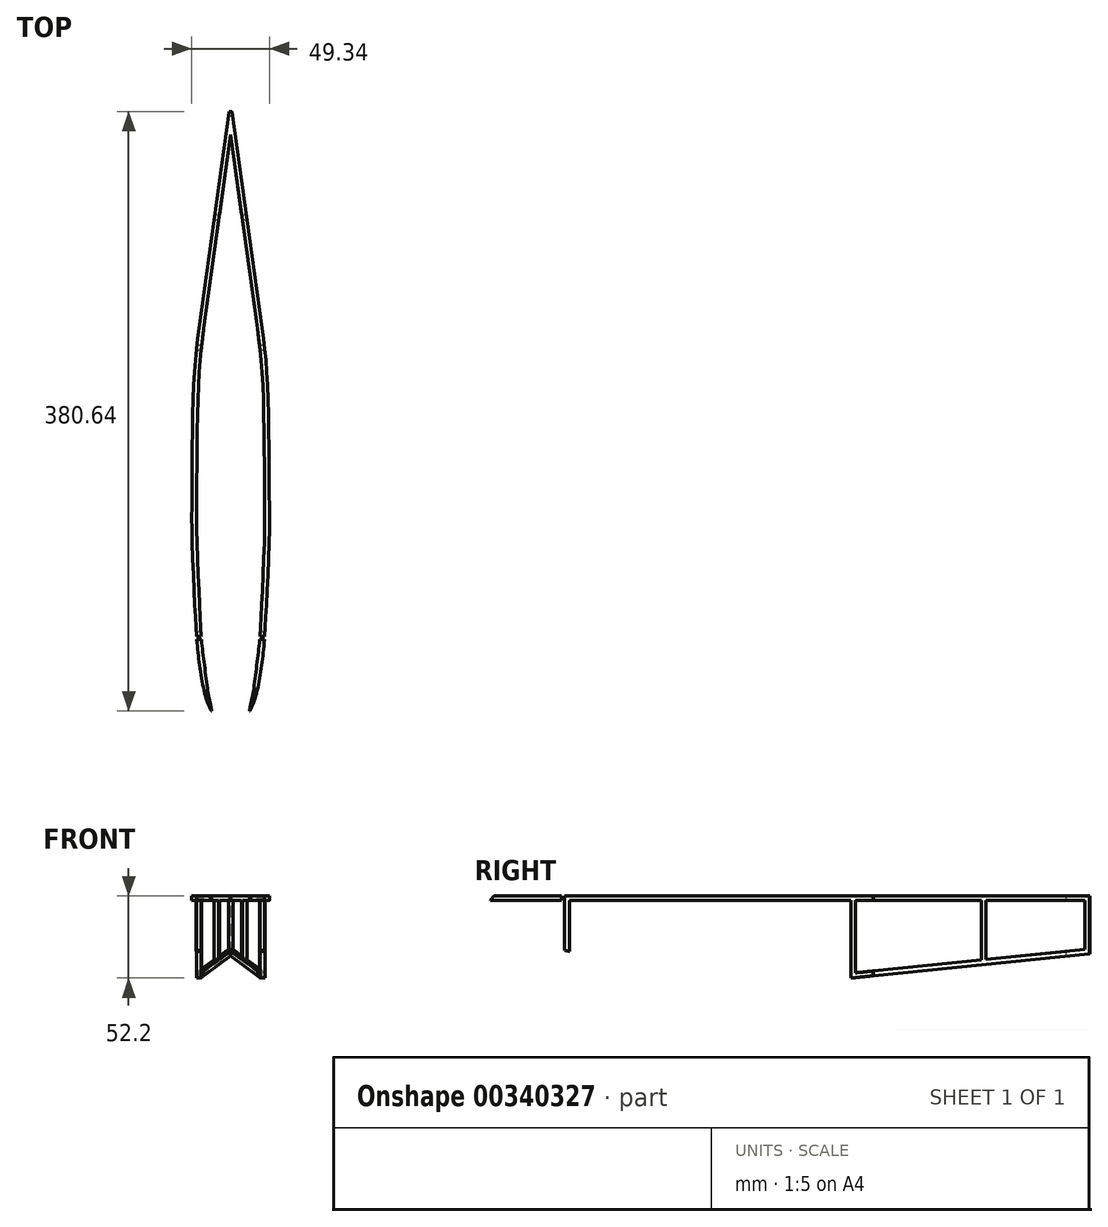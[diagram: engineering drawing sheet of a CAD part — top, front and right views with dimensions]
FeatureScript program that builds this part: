
annotation { "Feature Type Name" : "Feature", "Feature Type Description" : "" }
export const myFeature = defineFeature(function(context is Context, id is Id, definition is map)
    precondition{}
    {
        {
            var Q0;
            Q0=qCreatedBy(makeId("Right.planeOp"),FACE);
            var sketch = newSketch(context, id + "F0", { "sketchPlane" : qUnion([Q0])});
            skLineSegment(sketch, "E0", {"start": v(-181.67, 6.86) * mm, "end": v(153.75, 6.86) * mm});
            skLineSegment(sketch, "E1", {"start": v(153.75, 6.86) * mm, "end": v(153.75, -31.42) * mm});
            skLineSegment(sketch, "E2", {"start": v(153.75, -31.42) * mm, "end": v(2.12, -46.85) * mm});
            skLineSegment(sketch, "E3", {"start": v(-181.67, 6.86) * mm, "end": v(-181.67, -34.5) * mm});
            skLineSegment(sketch, "E4", {"start": v(-47.91, -2.8) * mm, "end": v(-7.67, -2.37) * mm});
            skLineSegment(sketch, "E5", {"start": v(-4.64, -5.37) * mm, "end": v(-4.64, -30.44) * mm});
            skLineSegment(sketch, "E6", {"start": v(-8.1, -33.4) * mm, "end": v(-48.4, -27.13) * mm});
            skLineSegment(sketch, "E7", {"start": v(-50.93, -24.15) * mm, "end": v(-50.88, -5.79) * mm});
            skPoint(sketch, "E8.visualSharp", {"position": v(-50.87, -2.83) * mm});
            skArc(sketch, "E8.filletArc", {"start": v(-47.91, -2.8) * mm, "mid": v(-50, -3.68) * mm, "end": v(-50.88, -5.79) * mm});
            skPoint(sketch, "E9.visualSharp", {"position": v(-50.94, -26.73) * mm});
            skArc(sketch, "E9.filletArc", {"start": v(-50.93, -24.15) * mm, "mid": v(-50.21, -26.11) * mm, "end": v(-48.4, -27.13) * mm});
            skPoint(sketch, "E10.visualSharp", {"position": v(-4.64, -33.95) * mm});
            skArc(sketch, "E10.filletArc", {"start": v(-8.1, -33.4) * mm, "mid": v(-5.69, -32.72) * mm, "end": v(-4.64, -30.44) * mm});
            skPoint(sketch, "E11.visualSharp", {"position": v(-4.64, -2.34) * mm});
            skArc(sketch, "E11.filletArc", {"start": v(-4.64, -5.37) * mm, "mid": v(-5.53, -3.24) * mm, "end": v(-7.67, -2.37) * mm});
            skLineSegment(sketch, "E12", {"start": v(-181.67, 3.86) * mm, "end": v(153.75, 3.86) * mm});
            skLineSegment(sketch, "E13", {"start": v(153.75, -26.9) * mm, "end": v(2.12, -42.32) * mm});
            skLineSegment(sketch, "E14", {"start": v(153.75, -29.91) * mm, "end": v(2.12, -45.34) * mm});
            skLineSegment(sketch, "E15", {"start": v(2.12, -45.34) * mm, "end": v(2.12, -42.32) * mm});
            skLineSegment(sketch, "E16", {"start": v(150.75, -27.2) * mm, "end": v(150.75, 3.86) * mm});
            skLineSegment(sketch, "E17", {"start": v(13.01, -5.1) * mm, "end": v(13.01, -30.7) * mm});
            skLineSegment(sketch, "E18", {"start": v(16.26, -33.7) * mm, "end": v(74.4, -28.8) * mm});
            skLineSegment(sketch, "E19", {"start": v(77.15, -25.8) * mm, "end": v(77.15, -4.88) * mm});
            skLineSegment(sketch, "E20", {"start": v(74.14, -1.88) * mm, "end": v(16, -2.1) * mm});
            skPoint(sketch, "E21.visualSharp", {"position": v(13.01, -2.12) * mm});
            skArc(sketch, "E21.filletArc", {"start": v(16, -2.1) * mm, "mid": v(13.88, -3) * mm, "end": v(13.01, -5.1) * mm});
            skPoint(sketch, "E22.visualSharp", {"position": v(13.01, -33.97) * mm});
            skArc(sketch, "E22.filletArc", {"start": v(13.01, -30.7) * mm, "mid": v(13.98, -32.92) * mm, "end": v(16.26, -33.7) * mm});
            skPoint(sketch, "E23.visualSharp", {"position": v(77.15, -28.57) * mm});
            skArc(sketch, "E23.filletArc", {"start": v(74.4, -28.8) * mm, "mid": v(76.36, -27.84) * mm, "end": v(77.15, -25.8) * mm});
            skPoint(sketch, "E24.visualSharp", {"position": v(77.15, -1.87) * mm});
            skArc(sketch, "E24.filletArc", {"start": v(77.15, -4.88) * mm, "mid": v(76.27, -2.76) * mm, "end": v(74.14, -1.88) * mm});
            skLineSegment(sketch, "E25", {"start": v(84.94, 3.86) * mm, "end": v(84.94, -33.9) * mm});
            skLineSegment(sketch, "E26", {"start": v(87.94, 3.86) * mm, "end": v(87.94, -33.6) * mm});
            skLineSegment(sketch, "E27", {"start": v(2.12, -46.85) * mm, "end": v(2.12, -45.34) * mm});
            skLineSegment(sketch, "E28", {"start": v(2.12, -42.32) * mm, "end": v(2.12, 3.86) * mm});
            skLineSegment(sketch, "E29", {"start": v(5.12, 3.86) * mm, "end": v(5.12, -42.02) * mm});
            skCircle(sketch, "E30", {"center": v(6.62, -40.36) * mm, "radius": 1.5 * mm});
            skArc(sketch, "E31", {"start": v(97.1, 2.65) * mm, "mid": v(95.55, 1.2) * mm, "end": v(97, -0.35) * mm});
            skArc(sketch, "E32", {"start": v(110.86, -0.85) * mm, "mid": v(112.4, 0.6) * mm, "end": v(110.97, 2.15) * mm});
            skLineSegment(sketch, "E33", {"start": v(97.1, 2.65) * mm, "end": v(110.97, 2.15) * mm});
            skLineSegment(sketch, "E34", {"start": v(97, -0.35) * mm, "end": v(110.86, -0.85) * mm});
            skLineSegment(sketch, "E35", {"start": v(96.15, -6.4) * mm, "end": v(96.15, -23.76) * mm});
            skLineSegment(sketch, "E36", {"start": v(99.4, -26.75) * mm, "end": v(141.55, -23.37) * mm});
            skLineSegment(sketch, "E37", {"start": v(144.3, -20.38) * mm, "end": v(144.3, -6.7) * mm});
            skLineSegment(sketch, "E38", {"start": v(141.33, -3.7) * mm, "end": v(99.17, -3.4) * mm});
            skPoint(sketch, "E39.visualSharp", {"position": v(96.15, -3.38) * mm});
            skArc(sketch, "E39.filletArc", {"start": v(99.17, -3.4) * mm, "mid": v(97.04, -4.28) * mm, "end": v(96.15, -6.4) * mm});
            skPoint(sketch, "E40.visualSharp", {"position": v(96.15, -27) * mm});
            skArc(sketch, "E40.filletArc", {"start": v(96.15, -23.76) * mm, "mid": v(97.12, -25.96) * mm, "end": v(99.4, -26.75) * mm});
            skPoint(sketch, "E41.visualSharp", {"position": v(144.3, -23.15) * mm});
            skArc(sketch, "E41.filletArc", {"start": v(141.55, -23.37) * mm, "mid": v(143.51, -22.42) * mm, "end": v(144.3, -20.38) * mm});
            skPoint(sketch, "E42.visualSharp", {"position": v(144.3, -3.72) * mm});
            skArc(sketch, "E42.filletArc", {"start": v(144.3, -6.7) * mm, "mid": v(143.44, -4.58) * mm, "end": v(141.33, -3.7) * mm});
            skLineSegment(sketch, "E43", {"start": v(2.12, -46.85) * mm, "end": v(-9.88, -46.85) * mm});
            skLineSegment(sketch, "E44", {"start": v(-9.88, -46.85) * mm, "end": v(-9.88, -43.2) * mm});
            skLineSegment(sketch, "E45", {"start": v(-9.88, -43.2) * mm, "end": v(2.12, -45.58) * mm});
            skFitSpline(sketch, "E46", {"points": [v(-9.88, -46.85) * mm, v(-40, -44.73) * mm, v(-64.24, -44) * mm, v(-84.8, -44.39) * mm, v(-104.96, -46.05) * mm, v(-118.28, -46.24) * mm, v(-121.99, -46) * mm, v(-124.1, -45.33) * mm, v(-125.1, -44.5) * mm, v(-125.49, -43.66) * mm, v(-125.03, -42.58) * mm, v(-121.9, -40.97) * mm, v(-115.8, -39) * mm, v(-104.8, -36.68) * mm, v(-87.72, -34.92) * mm, v(-76.3, -34.78) * mm, v(-62.3, -35.33) * mm, v(-45.44, -37.09) * mm, v(-20.64, -41.08) * mm, v(-9.88, -43.2) * mm], "startDerivative": vector(-343.17, 26.9) * mm, "endDerivative": vector(173.05, -35.78) * mm});
            skLineSegment(sketch, "E47", {"start": v(-119.74, -40.2) * mm, "end": v(-119.74, -46.2) * mm});
            skLineSegment(sketch, "E48", {"start": v(-125.49, 3.86) * mm, "end": v(-125.49, -43.66) * mm});
            skLineSegment(sketch, "E49.bottom", {"start": v(-111.2, -2.56) * mm, "end": v(-72.11, -2.56) * mm});
            skLineSegment(sketch, "E49.top", {"start": v(-111.2, -27.34) * mm, "end": v(-72.11, -27.34) * mm});
            skLineSegment(sketch, "E49.left", {"start": v(-114.2, -5.56) * mm, "end": v(-114.2, -24.34) * mm});
            skLineSegment(sketch, "E49.right", {"start": v(-69.11, -5.56) * mm, "end": v(-69.11, -24.34) * mm});
            skPoint(sketch, "E50.visualSharp", {"position": v(-114.2, -2.56) * mm});
            skArc(sketch, "E50.filletArc", {"start": v(-111.2, -2.56) * mm, "mid": v(-113.32, -3.44) * mm, "end": v(-114.2, -5.56) * mm});
            skPoint(sketch, "E51.visualSharp", {"position": v(-114.2, -27.34) * mm});
            skArc(sketch, "E51.filletArc", {"start": v(-114.2, -24.34) * mm, "mid": v(-113.32, -26.46) * mm, "end": v(-111.2, -27.34) * mm});
            skPoint(sketch, "E52.visualSharp", {"position": v(-69.11, -27.34) * mm});
            skArc(sketch, "E52.filletArc", {"start": v(-72.11, -27.34) * mm, "mid": v(-69.99, -26.46) * mm, "end": v(-69.11, -24.34) * mm});
            skPoint(sketch, "E53.visualSharp", {"position": v(-69.11, -2.56) * mm});
            skArc(sketch, "E53.filletArc", {"start": v(-69.11, -5.56) * mm, "mid": v(-69.99, -3.44) * mm, "end": v(-72.11, -2.56) * mm});
            skLineSegment(sketch, "E54", {"start": v(-55.36, 3.86) * mm, "end": v(-55.36, -35.9) * mm});
            skLineSegment(sketch, "E55", {"start": v(-57.36, 3.86) * mm, "end": v(-57.36, -35.7) * mm});
            skFitSpline(sketch, "E56", {"points": [v(2.12, -40.57) * mm, v(-16.08, -36.4) * mm, v(-46.24, -31.25) * mm, v(-69.78, -29.1) * mm, v(-81.85, -28.82) * mm, v(-101.5, -30.15) * mm, v(-112.18, -32.12) * mm, v(-119.26, -34.2) * mm, v(-125.49, -36.64) * mm], "startDerivative": vector(-122.16, 29.48) * mm, "endDerivative": vector(-74.05, -30.55) * mm});
            skLineSegment(sketch, "E57", {"start": v(-77.75, -34.76) * mm, "end": v(-77.75, -38.76) * mm});
            skLineSegment(sketch, "E58", {"start": v(-77.75, -38.76) * mm, "end": v(-73.75, -38.76) * mm});
            skLineSegment(sketch, "E59", {"start": v(-73.75, -38.76) * mm, "end": v(-73.75, -34.84) * mm});
            skLineSegment(sketch, "E60", {"start": v(-179.67, 3.86) * mm, "end": v(-179.67, -35.22) * mm});
            skLineSegment(sketch, "E61", {"start": v(-127.49, 3.86) * mm, "end": v(-127.49, -45.88) * mm});
            skLineSegment(sketch, "E62", {"start": v(-127.49, -38.43) * mm, "end": v(-179.67, -27.75) * mm});
            skCircle(sketch, "E63", {"center": v(-128.99, -36.6) * mm, "radius": 1.5 * mm});
            skLineSegment(sketch, "E64", {"start": v(-176.67, 3.86) * mm, "end": v(-176.67, -28.37) * mm});
            skLineSegment(sketch, "E65", {"start": v(-181.67, 6.86) * mm, "end": v(-181.67, 19.81) * mm});
            skLineSegment(sketch, "E66", {"start": v(-181.67, 19.81) * mm, "end": v(-179.67, 19.81) * mm});
            skLineSegment(sketch, "E67", {"start": v(-179.67, 19.81) * mm, "end": v(-179.67, 6.86) * mm});
            skLineSegment(sketch, "E68", {"start": v(-179.67, 6.86) * mm, "end": v(-179.67, 3.86) * mm});
            skLineSegment(sketch, "E69", {"start": v(-179.67, 19.81) * mm, "end": v(-58.12, 19.81) * mm});
            skFitSpline(sketch, "E70", {"points": [v(-58.12, 19.81) * mm, v(-55.87, 16.49) * mm, v(-51.87, 13.82) * mm, v(-44.68, 11.1) * mm, v(-38.76, 9.83) * mm, v(-34.72, 9.5) * mm, v(-32.9, 9.46) * mm, v(-31.68, 8.98) * mm, v(-31.2, 8.18) * mm, v(-31.04, 6.86) * mm], "startDerivative": vector(15.95, -28.34) * mm, "endDerivative": vector(1.18, -19.42) * mm});
            skPoint(sketch, "E71.9.internal.snap0", {"position": v(-13.96, 6.86) * mm});
            skFitSpline(sketch, "E71", {"points": [v(-181.67, 19.81) * mm, v(-183.41, 18.39) * mm, v(-187.18, 16.28) * mm, v(-194, 13.94) * mm, v(-199.88, 12.47) * mm, v(-206.36, 11.53) * mm, v(-212.31, 11) * mm, v(-216.9, 10.25) * mm, v(-221.13, 8.93) * mm, v(-224.44, 6.86) * mm, v(-226.33, 4.9) * mm, v(-227.04, 3.36) * mm, v(-227.27, 0.8) * mm, v(-226.87, -1.76) * mm, v(-225.22, -5.47) * mm, v(-221.64, -10.05) * mm, v(-215.45, -15.6) * mm, v(-203.85, -23.7) * mm, v(-194.52, -28.9) * mm, v(-181.67, -34.5) * mm, v(-165.17, -39.5) * mm, v(-153.07, -41.9) * mm, v(-135.2, -44.8) * mm, v(-127.49, -45.88) * mm, v(-125.49, -46.02) * mm], "startDerivative": vector(-63.83, -56.2) * mm, "endDerivative": vector(74.87, -4.7) * mm});
            skLineSegment(sketch, "E72", {"start": v(-125.49, -46.02) * mm, "end": v(-125.49, -43.66) * mm});
            skLineSegment(sketch, "E73", {"start": v(-181.67, 6.86) * mm, "end": v(-224.44, 6.86) * mm});
            skLineSegment(sketch, "E74", {"start": v(-181.67, 3.86) * mm, "end": v(-226.89, 3.86) * mm});
            skLineSegment(sketch, "E75", {"start": v(-125.7, -48) * mm, "end": v(-131.67, -47.35) * mm});
            skLineSegment(sketch, "E76", {"start": v(-131.67, -47.35) * mm, "end": v(-131.45, -45.37) * mm});
            skLineSegment(sketch, "E77", {"start": v(-125.7, -48) * mm, "end": v(-125.49, -46.02) * mm});
            skFitSpline(sketch, "E78", {"points": [v(-125.49, -44.33) * mm, v(-127.49, -44.12) * mm, v(-140.7, -42.33) * mm, v(-160.51, -38.82) * mm, v(-171.33, -36.19) * mm, v(-179.67, -33.56) * mm, v(-181.67, -32.9) * mm], "startDerivative": vector(-19.3, 1.8) * mm, "endDerivative": vector(-19.46, 6.5) * mm});
            skFitSpline(sketch, "E79", {"points": [v(-181.67, -32.9) * mm, v(-188.4, -30.56) * mm, v(-198.45, -26.86) * mm], "startDerivative": vector(-14.26, 4.84) * mm, "endDerivative": vector(-19.1, 7.25) * mm});
            skLineSegment(sketch, "E80", {"start": v(-181.67, -18.47) * mm, "end": v(-214.55, -16.3) * mm});
            skLineSegment(sketch, "E81", {"start": v(-104.96, -46.05) * mm, "end": v(-9.88, -46.85) * mm});
            skLineSegment(sketch, "E82", {"start": v(153.75, 9.86) * mm, "end": v(153.75, 6.86) * mm});
            skLineSegment(sketch, "E83", {"start": v(153.75, 9.86) * mm, "end": v(76.63, 9.86) * mm});
            skArc(sketch, "E84", {"start": v(76.63, 9.86) * mm, "mid": v(75.13, 8.36) * mm, "end": v(76.63, 6.86) * mm});
            skFitSpline(sketch, "E85", {"points": [v(89.9, 9.86) * mm, v(58.05, 12.78) * mm, v(25.06, 16.1) * mm, v(1.18, 18.57) * mm], "startDerivative": vector(-90.45, 8.07) * mm, "endDerivative": vector(-75.96, 7.86) * mm});
            skFitSpline(sketch, "E86", {"points": [v(1.18, 18.57) * mm, v(0, 14.86) * mm, v(-1.7, 11.63) * mm, v(-3.87, 9.14) * mm, v(-6.2, 7.64) * mm, v(-7.3, 7.32) * mm, v(-8.32, 7.22) * mm, v(-9.2, 7.24) * mm, v(-9.58, 7.12) * mm, v(-9.7, 6.86) * mm], "startDerivative": vector(-6.18, -22.1) * mm, "endDerivative": vector(-1.74, -6.23) * mm});
            skFitSpline(sketch, "E87", {"points": [v(1.18, 18.57) * mm, v(0.28, 21.52) * mm, v(0.14, 24.9) * mm, v(0.78, 27.64) * mm, v(2.27, 29.53) * mm], "startDerivative": vector(-4.12, 11.13) * mm, "endDerivative": vector(7.44, 7.67) * mm});
            skFitSpline(sketch, "E88", {"points": [v(2.27, 29.53) * mm, v(11.3, 28.6) * mm, v(21.09, 26.4) * mm, v(32.75, 22.66) * mm, v(40.6, 19.5) * mm, v(54.25, 13.15) * mm], "startDerivative": vector(49.49, -3.82) * mm, "endDerivative": vector(62.92, -29.27) * mm});
            skLineSegment(sketch, "E89", {"start": v(153.75, 9.86) * mm, "end": v(153.75, 85.7) * mm});
            skLineSegment(sketch, "E90", {"start": v(99.78, 24.8) * mm, "end": v(129.82, 70.26) * mm});
            skArc(sketch, "E91.filletArc", {"start": v(72.01, 11.47) * mm, "mid": v(87.74, 14.3) * mm, "end": v(99.78, 24.8) * mm});
            skFitSpline(sketch, "E92", {"points": [v(129.82, 70.26) * mm, v(134.93, 77.14) * mm, v(141.98, 82.79) * mm, v(148.76, 85.27) * mm, v(153.75, 85.7) * mm, v(156.73, 85.2) * mm, v(160.62, 81.98) * mm, v(165.42, 74.96) * mm, v(172.68, 57.49) * mm, v(179.23, 32.24) * mm, v(182.93, 8.22) * mm, v(182.77, -12.22) * mm, v(181.56, -18.26) * mm, v(179.68, -22.66) * mm, v(175.84, -26.39) * mm, v(168.64, -29.04) * mm, v(160.77, -30.62) * mm, v(153.75, -31.42) * mm], "startDerivative": vector(82.95, 125.52) * mm, "endDerivative": vector(-116.11, -2.75) * mm});
            skCircle(sketch, "E93", {"center": v(167.62, 21.77) * mm, "radius": 7.19 * mm});
            skPoint(sketch, "E93.first.point", {"position": v(164.46, 15.31) * mm});
            skPoint(sketch, "E93.second.point", {"position": v(171.48, 27.83) * mm});
            skPoint(sketch, "E93.third.point", {"position": v(161.67, 25.8) * mm});
            skCircle(sketch, "E94", {"center": v(165.61, 40.53) * mm, "radius": 6.43 * mm});
            skPoint(sketch, "E94.first.point", {"position": v(160.32, 36.88) * mm});
            skPoint(sketch, "E94.second.point", {"position": v(171.99, 39.67) * mm});
            skPoint(sketch, "E94.third.point", {"position": v(165.14, 46.95) * mm});
            skCircle(sketch, "E95", {"center": v(162.35, 61.35) * mm, "radius": 4.5 * mm});
            skPoint(sketch, "E95.first.point", {"position": v(159.9, 65.13) * mm});
            skPoint(sketch, "E95.second.point", {"position": v(159.98, 57.52) * mm});
            skPoint(sketch, "E95.third.point", {"position": v(166.4, 59.38) * mm});
            skLineSegment(sketch, "E96", {"start": v(143.53, 53.67) * mm, "end": v(143.53, 24.67) * mm});
            skLineSegment(sketch, "E97", {"start": v(138.53, 19.67) * mm, "end": v(120.3, 19.67) * mm});
            skLineSegment(sketch, "E98", {"start": v(116.06, 27.33) * mm, "end": v(134.3, 56.33) * mm});
            skPoint(sketch, "E99.visualSharp", {"position": v(143.53, 19.67) * mm});
            skArc(sketch, "E99.filletArc", {"start": v(138.53, 19.67) * mm, "mid": v(142.06, 21.13) * mm, "end": v(143.53, 24.67) * mm});
            skPoint(sketch, "E100.visualSharp", {"position": v(143.53, 71.02) * mm});
            skArc(sketch, "E100.filletArc", {"start": v(143.53, 53.67) * mm, "mid": v(139.91, 58.48) * mm, "end": v(134.3, 56.33) * mm});
            skPoint(sketch, "E101.visualSharp", {"position": v(111.25, 19.67) * mm});
            skArc(sketch, "E101.filletArc", {"start": v(116.06, 27.33) * mm, "mid": v(115.92, 22.25) * mm, "end": v(120.3, 19.67) * mm});
            skLineSegment(sketch, "E102", {"start": v(-23.06, 48.92) * mm, "end": v(-35.06, 48.92) * mm});
            skLineSegment(sketch, "E103", {"start": v(-35.06, 48.92) * mm, "end": v(-35.06, 52.57) * mm});
            skLineSegment(sketch, "E104", {"start": v(-35.06, 52.57) * mm, "end": v(-23.06, 50.19) * mm});
            skFitSpline(sketch, "E105", {"points": [v(-35.06, 48.92) * mm, v(-65.2, 51.03) * mm, v(-89.43, 51.77) * mm, v(-109.98, 51.38) * mm, v(-130.15, 49.72) * mm, v(-143.47, 49.53) * mm, v(-147.18, 49.76) * mm, v(-149.28, 50.44) * mm, v(-150.28, 51.26) * mm, v(-150.67, 52.1) * mm, v(-150.22, 53.19) * mm, v(-147.09, 54.8) * mm, v(-140.98, 56.77) * mm, v(-129.99, 59.09) * mm, v(-112.91, 60.84) * mm, v(-101.49, 60.99) * mm, v(-87.49, 60.44) * mm, v(-70.62, 58.68) * mm, v(-45.83, 54.69) * mm, v(-35.06, 52.57) * mm], "startDerivative": vector(-343.17, 26.9) * mm, "endDerivative": vector(173.05, -35.78) * mm});
            skLineSegment(sketch, "E106", {"start": v(-144.93, 55.56) * mm, "end": v(-144.93, 49.56) * mm});
            skLineSegment(sketch, "E107", {"start": v(-102.93, 61.01) * mm, "end": v(-102.93, 57.01) * mm});
            skLineSegment(sketch, "E108", {"start": v(-102.93, 57.01) * mm, "end": v(-98.93, 57.01) * mm});
            skLineSegment(sketch, "E109", {"start": v(-98.93, 57.01) * mm, "end": v(-98.93, 60.93) * mm});
            skFitSpline(sketch, "E110", {"points": [v(-150.67, 52.1) * mm, v(-150.67, 49.9) * mm, v(-149.37, 47.55) * mm, v(-146.82, 46.07) * mm, v(-144.27, 45.53) * mm, v(-142.46, 45.46) * mm], "startDerivative": vector(-1.24, -11.47) * mm, "endDerivative": vector(10.07, -0.04) * mm});
            skLineSegment(sketch, "E111", {"start": v(-142.46, 45.46) * mm, "end": v(-27.07, 45.46) * mm});
            skLineSegment(sketch, "E112", {"start": v(-23.06, 50.19) * mm, "end": v(-23.06, 48.92) * mm});
            skFitSpline(sketch, "E113", {"points": [v(-27.07, 45.46) * mm, v(-25.21, 45.85) * mm, v(-23.67, 47.07) * mm, v(-23.06, 48.92) * mm], "startDerivative": vector(5.72, 0.63) * mm, "endDerivative": vector(1.14, 5.89) * mm});
            skLineSegment(sketch, "E114", {"start": v(-142.8, 49.52) * mm, "end": v(-121.7, -27.63) * mm});
            skLineSegment(sketch, "E115", {"start": v(-137.6, 49.5) * mm, "end": v(-116.88, -26.3) * mm});
            skArc(sketch, "E116", {"start": v(-121.7, -27.63) * mm, "mid": v(-118.63, -29.38) * mm, "end": v(-116.88, -26.3) * mm});
            skArc(sketch, "E117", {"start": v(-58.49, -24.2) * mm, "mid": v(-55.4, -25.93) * mm, "end": v(-53.68, -22.85) * mm});
            skLineSegment(sketch, "E118", {"start": v(-79.88, 51.6) * mm, "end": v(-58.49, -24.2) * mm});
            skLineSegment(sketch, "E119", {"start": v(-53.68, -22.85) * mm, "end": v(-74.64, 51.44) * mm});
            skSolve(sketch);
        }
        {
            var Q0;
            {var subQ0=sQuery(id+"F0.wireOp",EDGE,"E48");var subQ1=sQuery(id+"F0.wireOp",EDGE,"E46");var subQ3=makeQuery(id+"F0.imprint","INTERSECT",VERTEX,{"derivedFrom":[subQ1,subQ0]});Q0=makeQuery(id+"F0.imprint","IMPRINT",FACE,{"disambiguationData":[TD([[makeQuery(id+"F0.imprint","IMPRINT",EDGE,{"disambiguationData":[TD([[subQ3,1.0]])],"derivedFrom":subQ1}),-1.0]])]});}
            var Q1;
            {var subQ0=sQuery(id+"F0.wireOp",EDGE,"E73");Q1=makeQuery(id+"F0.imprint","IMPRINT",FACE,{"disambiguationData":[TD([[makeQuery(id+"F0.imprint","IMPRINT",EDGE,{"derivedFrom":subQ0}),1.0]])]});}
            var Q2;
            {var subQ0=sQuery(id+"F0.wireOp",EDGE,"E79");Q2=makeQuery(id+"F0.imprint","IMPRINT",FACE,{"disambiguationData":[TD([[makeQuery(id+"F0.imprint","IMPRINT",EDGE,{"derivedFrom":subQ0}),-1.0]])]});}
            var Q3;
            {var subQ0=sQuery(id+"F0.wireOp",EDGE,"E74");Q3=makeQuery(id+"F0.imprint","IMPRINT",FACE,{"disambiguationData":[TD([[makeQuery(id+"F0.imprint","IMPRINT",EDGE,{"derivedFrom":subQ0}),1.0]])]});}
            var Q4;
            {var subQ0=sQuery(id+"F0.wireOp",EDGE,"E60");var subQ3=makeQuery(id+"F0.imprint","INTERSECT",VERTEX,{"derivedFrom":[subQ0,sQuery(id+"F0.wireOp",EDGE,"E62")]});Q4=makeQuery(id+"F0.imprint","IMPRINT",FACE,{"disambiguationData":[TD([[makeQuery(id+"F0.imprint","IMPRINT",EDGE,{"disambiguationData":[TD([[subQ3,-1.0]])],"derivedFrom":subQ0}),-1.0]])]});}
            var Q5;
            {var subQ0=sQuery(id+"F0.wireOp",EDGE,"E62");var subQ6=sQuery(id+"F0.wireOp",EDGE,"E60");var subQ9=makeQuery(id+"F0.imprint","INTERSECT",VERTEX,{"derivedFrom":[subQ6,subQ0]});Q5=makeQuery(id+"F0.imprint","IMPRINT",FACE,{"disambiguationData":[TD([[makeQuery(id+"F0.imprint","IMPRINT",EDGE,{"disambiguationData":[TD([[subQ9,-1.0]])],"derivedFrom":subQ6}),1.0]])]});}
            var Q6;
            {var subQ3=sQuery(id+"F0.wireOp",EDGE,"E64");Q6=makeQuery(id+"F0.imprint","IMPRINT",FACE,{"disambiguationData":[TD([[makeQuery(id+"F0.imprint","IMPRINT",EDGE,{"derivedFrom":subQ3}),-1.0]])]});}
            var Q7;
            {var subQ3=sQuery(id+"F0.wireOp",EDGE,"E68");Q7=makeQuery(id+"F0.imprint","IMPRINT",FACE,{"disambiguationData":[TD([[makeQuery(id+"F0.imprint","IMPRINT",EDGE,{"derivedFrom":subQ3}),-1.0]])]});}
            var Q8;
            {var subQ0=sQuery(id+"F0.wireOp",EDGE,"E68");Q8=makeQuery(id+"F0.imprint","IMPRINT",FACE,{"disambiguationData":[TD([[makeQuery(id+"F0.imprint","IMPRINT",EDGE,{"derivedFrom":subQ0}),1.0]])]});}
            var Q9;
            {var subQ5=sQuery(id+"F0.wireOp",EDGE,"E64");Q9=makeQuery(id+"F0.imprint","IMPRINT",FACE,{"disambiguationData":[TD([[makeQuery(id+"F0.imprint","IMPRINT",EDGE,{"derivedFrom":subQ5}),1.0]])]});}
            var Q10;
            {var subQ5=sQuery(id+"F0.wireOp",EDGE,"E114");var subQ6=sQuery(id+"F0.wireOp",EDGE,"E0");var subQ7=makeQuery(id+"F0.imprint","INTERSECT",VERTEX,{"derivedFrom":[subQ6,subQ5]});Q10=makeQuery(id+"F0.imprint","IMPRINT",FACE,{"disambiguationData":[TD([[makeQuery(id+"F0.imprint","IMPRINT",EDGE,{"disambiguationData":[TD([[subQ7,-1.0]])],"derivedFrom":subQ6}),-1.0]])]});}
            var Q11;
            {var subQ0=sQuery(id+"F0.wireOp",EDGE,"E61");var subQ1=sQuery(id+"F0.wireOp",EDGE,"E12");var subQ2=makeQuery(id+"F0.imprint","INTERSECT",VERTEX,{"derivedFrom":[subQ1,subQ0]});Q11=makeQuery(id+"F0.imprint","IMPRINT",FACE,{"disambiguationData":[TD([[makeQuery(id+"F0.imprint","IMPRINT",EDGE,{"disambiguationData":[TD([[subQ2,1.0]])],"derivedFrom":subQ1}),-1.0]])]});}
            var Q12;
            {var subQ0=sQuery(id+"F0.wireOp",EDGE,"E48");var subQ1=sQuery(id+"F0.wireOp",EDGE,"E12");var subQ2=makeQuery(id+"F0.imprint","INTERSECT",VERTEX,{"derivedFrom":[subQ1,subQ0]});Q12=makeQuery(id+"F0.imprint","IMPRINT",FACE,{"disambiguationData":[TD([[makeQuery(id+"F0.imprint","IMPRINT",EDGE,{"disambiguationData":[TD([[subQ2,1.0]])],"derivedFrom":subQ1}),-1.0]])]});}
            var Q13;
            {var subQ0=sQuery(id+"F0.wireOp",EDGE,"E116");Q13=makeQuery(id+"F0.imprint","IMPRINT",FACE,{"disambiguationData":[TD([[makeQuery(id+"F0.imprint","IMPRINT",EDGE,{"derivedFrom":subQ0}),1.0]])]});}
            var Q14;
            {var subQ4=sQuery(id+"F0.wireOp",EDGE,"E48");var subQ5=makeQuery(id+"F0.imprint","INTERSECT",VERTEX,{"derivedFrom":[subQ4,sQuery(id+"F0.wireOp",EDGE,"E56")]});Q14=makeQuery(id+"F0.imprint","IMPRINT",FACE,{"disambiguationData":[TD([[makeQuery(id+"F0.imprint","IMPRINT",EDGE,{"disambiguationData":[TD([[subQ5,1.0]])],"derivedFrom":subQ4}),-1.0]])]});}
            var Q15;
            Q15=makeQuery(id+"F0.imprint","IMPRINT",FACE,{"disambiguationData":[TD([[makeQuery(id+"F0.imprint","IMPRINT",EDGE,{"derivedFrom":sQuery(id+"F0.wireOp",EDGE,"E49.bottom")}),1.0]])]});
            var Q16;
            {var subQ1=sQuery(id+"F0.wireOp",EDGE,"E46");var subQ5=makeQuery(id+"F0.imprint","INTERSECT",VERTEX,{"disambiguationData":[OD(0.0)],"derivedFrom":[subQ1,sQuery(id+"F0.wireOp",EDGE,"E47")]});Q16=makeQuery(id+"F0.imprint","IMPRINT",FACE,{"disambiguationData":[TD([[makeQuery(id+"F0.imprint","IMPRINT",EDGE,{"disambiguationData":[TD([[subQ5,1.0]])],"derivedFrom":subQ1}),1.0]])]});}
            var Q17;
            {var subQ0=sQuery(id+"F0.wireOp",EDGE,"E115");var subQ1=sQuery(id+"F0.wireOp",EDGE,"E0");var subQ2=makeQuery(id+"F0.imprint","INTERSECT",VERTEX,{"derivedFrom":[subQ1,subQ0]});Q17=makeQuery(id+"F0.imprint","IMPRINT",FACE,{"disambiguationData":[TD([[makeQuery(id+"F0.imprint","IMPRINT",EDGE,{"disambiguationData":[TD([[subQ2,-1.0]])],"derivedFrom":subQ1}),-1.0]])]});}
            var Q18;
            {var subQ0=sQuery(id+"F0.wireOp",EDGE,"E118");var subQ3=sQuery(id+"F0.wireOp",EDGE,"E12");var subQ4=makeQuery(id+"F0.imprint","INTERSECT",VERTEX,{"derivedFrom":[subQ3,subQ0]});Q18=makeQuery(id+"F0.imprint","IMPRINT",FACE,{"disambiguationData":[TD([[makeQuery(id+"F0.imprint","IMPRINT",EDGE,{"disambiguationData":[TD([[subQ4,-1.0]])],"derivedFrom":subQ3}),-1.0]])]});}
            var Q19;
            {var subQ0=sQuery(id+"F0.wireOp",EDGE,"E118");var subQ1=sQuery(id+"F0.wireOp",EDGE,"E0");var subQ2=makeQuery(id+"F0.imprint","INTERSECT",VERTEX,{"derivedFrom":[subQ1,subQ0]});Q19=makeQuery(id+"F0.imprint","IMPRINT",FACE,{"disambiguationData":[TD([[makeQuery(id+"F0.imprint","IMPRINT",EDGE,{"disambiguationData":[TD([[subQ2,-1.0]])],"derivedFrom":subQ1}),-1.0]])]});}
            var Q20;
            {var subQ8=sQuery(id+"F0.wireOp",EDGE,"E0");var subQ12=makeQuery(id+"F0.imprint","INTERSECT",VERTEX,{"derivedFrom":[subQ8,sQuery(id+"F0.wireOp",EDGE,"E70")]});Q20=makeQuery(id+"F0.imprint","IMPRINT",FACE,{"disambiguationData":[TD([[makeQuery(id+"F0.imprint","IMPRINT",EDGE,{"disambiguationData":[TD([[subQ12,1.0]])],"derivedFrom":subQ8}),-1.0]])]});}
            var Q21;
            {var subQ0=sQuery(id+"F0.wireOp",EDGE,"E55");var subQ1=sQuery(id+"F0.wireOp",EDGE,"E12");var subQ2=makeQuery(id+"F0.imprint","INTERSECT",VERTEX,{"derivedFrom":[subQ1,subQ0]});Q21=makeQuery(id+"F0.imprint","IMPRINT",FACE,{"disambiguationData":[TD([[makeQuery(id+"F0.imprint","IMPRINT",EDGE,{"disambiguationData":[TD([[subQ2,1.0]])],"derivedFrom":subQ1}),-1.0]])]});}
            var Q22;
            {var subQ0=sQuery(id+"F0.wireOp",EDGE,"E54");var subQ1=sQuery(id+"F0.wireOp",EDGE,"E12");var subQ2=makeQuery(id+"F0.imprint","INTERSECT",VERTEX,{"derivedFrom":[subQ1,subQ0]});Q22=makeQuery(id+"F0.imprint","IMPRINT",FACE,{"disambiguationData":[TD([[makeQuery(id+"F0.imprint","IMPRINT",EDGE,{"disambiguationData":[TD([[subQ2,1.0]])],"derivedFrom":subQ1}),-1.0]])]});}
            var Q23;
            {var subQ0=sQuery(id+"F0.wireOp",EDGE,"E119");var subQ1=sQuery(id+"F0.wireOp",EDGE,"E54");var subQ2=makeQuery(id+"F0.imprint","INTERSECT",VERTEX,{"derivedFrom":[subQ1,subQ0]});Q23=makeQuery(id+"F0.imprint","IMPRINT",FACE,{"disambiguationData":[TD([[makeQuery(id+"F0.imprint","IMPRINT",EDGE,{"disambiguationData":[TD([[subQ2,-1.0]])],"derivedFrom":subQ1}),-1.0]])]});}
            var Q24;
            {var subQ0=sQuery(id+"F0.wireOp",EDGE,"E54");var subQ1=sQuery(id+"F0.wireOp",EDGE,"E46");var subQ2=makeQuery(id+"F0.imprint","INTERSECT",VERTEX,{"derivedFrom":[subQ1,subQ0]});Q24=makeQuery(id+"F0.imprint","IMPRINT",FACE,{"disambiguationData":[TD([[makeQuery(id+"F0.imprint","IMPRINT",EDGE,{"disambiguationData":[TD([[subQ2,1.0]])],"derivedFrom":subQ1}),1.0]])]});}
            var Q25;
            {var subQ0=sQuery(id+"F0.wireOp",EDGE,"E117");var subQ1=sQuery(id+"F0.wireOp",EDGE,"E54");var subQ2=makeQuery(id+"F0.imprint","INTERSECT",VERTEX,{"derivedFrom":[subQ1,subQ0]});Q25=makeQuery(id+"F0.imprint","IMPRINT",FACE,{"disambiguationData":[TD([[makeQuery(id+"F0.imprint","IMPRINT",EDGE,{"disambiguationData":[TD([[subQ2,-1.0]])],"derivedFrom":subQ1}),-1.0]])]});}
            var Q26;
            Q26=makeQuery(id+"F0.imprint","IMPRINT",FACE,{"disambiguationData":[TD([[makeQuery(id+"F0.imprint","IMPRINT",EDGE,{"derivedFrom":sQuery(id+"F0.wireOp",EDGE,"E4")}),1.0]])]});
            var Q27;
            {var subQ0=sQuery(id+"F0.wireOp",EDGE,"E119");var subQ1=sQuery(id+"F0.wireOp",EDGE,"E54");var subQ2=makeQuery(id+"F0.imprint","INTERSECT",VERTEX,{"derivedFrom":[subQ1,subQ0]});Q27=makeQuery(id+"F0.imprint","IMPRINT",FACE,{"disambiguationData":[TD([[makeQuery(id+"F0.imprint","IMPRINT",EDGE,{"disambiguationData":[TD([[subQ2,-1.0]])],"derivedFrom":subQ1}),1.0]])]});}
            var Q28;
            {var subQ2=sQuery(id+"F0.wireOp",EDGE,"E15");Q28=makeQuery(id+"F0.imprint","IMPRINT",FACE,{"disambiguationData":[TD([[makeQuery(id+"F0.imprint","IMPRINT",EDGE,{"derivedFrom":subQ2}),1.0]])]});}
            var Q29;
            {var subQ5=sQuery(id+"F0.wireOp",EDGE,"E14");Q29=makeQuery(id+"F0.imprint","IMPRINT",FACE,{"disambiguationData":[TD([[makeQuery(id+"F0.imprint","IMPRINT",EDGE,{"derivedFrom":subQ5}),-1.0]])]});}
            var Q30;
            {var subQ0=sQuery(id+"F0.wireOp",EDGE,"E28");var subQ1=sQuery(id+"F0.wireOp",EDGE,"E12");var subQ2=makeQuery(id+"F0.imprint","INTERSECT",VERTEX,{"derivedFrom":[subQ1,subQ0]});Q30=makeQuery(id+"F0.imprint","IMPRINT",FACE,{"disambiguationData":[TD([[makeQuery(id+"F0.imprint","IMPRINT",EDGE,{"disambiguationData":[TD([[subQ2,-1.0]])],"derivedFrom":subQ1}),-1.0]])]});}
            var Q31;
            Q31=makeQuery(id+"F0.imprint","IMPRINT",FACE,{"disambiguationData":[TD([[makeQuery(id+"F0.imprint","IMPRINT",EDGE,{"derivedFrom":sQuery(id+"F0.wireOp",EDGE,"E17")}),-1.0]])]});
            var Q32;
            {var subQ0=sQuery(id+"F0.wireOp",EDGE,"E29");var subQ1=sQuery(id+"F0.wireOp",EDGE,"E13");var subQ2=makeQuery(id+"F0.imprint","INTERSECT",VERTEX,{"derivedFrom":[subQ1,subQ0]});Q32=makeQuery(id+"F0.imprint","IMPRINT",FACE,{"disambiguationData":[TD([[makeQuery(id+"F0.imprint","IMPRINT",EDGE,{"disambiguationData":[TD([[subQ2,1.0]])],"derivedFrom":subQ1}),-1.0]])]});}
            var Q33;
            {var subQ0=sQuery(id+"F0.wireOp",EDGE,"E62");var subQ1=sQuery(id+"F0.wireOp",EDGE,"E61");var subQ2=makeQuery(id+"F0.imprint","INTERSECT",VERTEX,{"derivedFrom":[subQ1,subQ0]});Q33=makeQuery(id+"F0.imprint","IMPRINT",FACE,{"disambiguationData":[TD([[makeQuery(id+"F0.imprint","IMPRINT",EDGE,{"disambiguationData":[TD([[subQ2,1.0]])],"derivedFrom":subQ1}),-1.0]])]});}
            var Q34;
            {var subQ0=sQuery(id+"F0.wireOp",EDGE,"E16");Q34=makeQuery(id+"F0.imprint","IMPRINT",FACE,{"disambiguationData":[TD([[makeQuery(id+"F0.imprint","IMPRINT",EDGE,{"derivedFrom":subQ0}),1.0]])]});}
            var Q35;
            {var subQ0=sQuery(id+"F0.wireOp",EDGE,"E25");Q35=makeQuery(id+"F0.imprint","IMPRINT",FACE,{"disambiguationData":[TD([[makeQuery(id+"F0.imprint","IMPRINT",EDGE,{"derivedFrom":subQ0}),1.0]])]});}
            var Q36;
            {var subQ5=sQuery(id+"F0.wireOp",EDGE,"E16");Q36=makeQuery(id+"F0.imprint","IMPRINT",FACE,{"disambiguationData":[TD([[makeQuery(id+"F0.imprint","IMPRINT",EDGE,{"derivedFrom":subQ5}),-1.0]])]});}
            extrude(context, id + "F1", {"entities" : qUnion([Q0, Q1, Q2, Q3, Q4, Q5, Q6, Q7, Q8, Q9, Q10, Q11, Q12, Q13, Q14, Q15, Q16, Q17, Q18, Q19, Q20, Q21, Q22, Q23, Q24, Q25, Q26, Q27, Q28, Q29, Q30, Q31, Q32, Q33, Q34, Q35, Q36]), "depth" : 1.5 * mm});
        }
        {
            var Q0;
            {var subQ0=sQuery(id+"F0.wireOp",EDGE,"E48");var subQ1=sQuery(id+"F0.wireOp",EDGE,"E46");var subQ3=makeQuery(id+"F0.imprint","INTERSECT",VERTEX,{"derivedFrom":[subQ1,subQ0]});Q0=makeQuery(id+"F0.imprint","IMPRINT",FACE,{"disambiguationData":[TD([[makeQuery(id+"F0.imprint","IMPRINT",EDGE,{"disambiguationData":[TD([[subQ3,1.0]])],"derivedFrom":subQ1}),-1.0]])]});}
            var Q1;
            {var subQ0=sQuery(id+"F0.wireOp",EDGE,"E73");Q1=makeQuery(id+"F0.imprint","IMPRINT",FACE,{"disambiguationData":[TD([[makeQuery(id+"F0.imprint","IMPRINT",EDGE,{"derivedFrom":subQ0}),1.0]])]});}
            var Q2;
            {var subQ0=sQuery(id+"F0.wireOp",EDGE,"E74");Q2=makeQuery(id+"F0.imprint","IMPRINT",FACE,{"disambiguationData":[TD([[makeQuery(id+"F0.imprint","IMPRINT",EDGE,{"derivedFrom":subQ0}),1.0]])]});}
            var Q3;
            {var subQ0=sQuery(id+"F0.wireOp",EDGE,"E79");Q3=makeQuery(id+"F0.imprint","IMPRINT",FACE,{"disambiguationData":[TD([[makeQuery(id+"F0.imprint","IMPRINT",EDGE,{"derivedFrom":subQ0}),-1.0]])]});}
            var Q4;
            {var subQ4=sQuery(id+"F0.wireOp",EDGE,"E48");var subQ5=makeQuery(id+"F0.imprint","INTERSECT",VERTEX,{"derivedFrom":[subQ4,sQuery(id+"F0.wireOp",EDGE,"E56")]});Q4=makeQuery(id+"F0.imprint","IMPRINT",FACE,{"disambiguationData":[TD([[makeQuery(id+"F0.imprint","IMPRINT",EDGE,{"disambiguationData":[TD([[subQ5,1.0]])],"derivedFrom":subQ4}),-1.0]])]});}
            var Q5;
            {var subQ8=sQuery(id+"F0.wireOp",EDGE,"E0");var subQ12=makeQuery(id+"F0.imprint","INTERSECT",VERTEX,{"derivedFrom":[subQ8,sQuery(id+"F0.wireOp",EDGE,"E70")]});Q5=makeQuery(id+"F0.imprint","IMPRINT",FACE,{"disambiguationData":[TD([[makeQuery(id+"F0.imprint","IMPRINT",EDGE,{"disambiguationData":[TD([[subQ12,1.0]])],"derivedFrom":subQ8}),-1.0]])]});}
            var Q6;
            {var subQ0=sQuery(id+"F0.wireOp",EDGE,"E68");Q6=makeQuery(id+"F0.imprint","IMPRINT",FACE,{"disambiguationData":[TD([[makeQuery(id+"F0.imprint","IMPRINT",EDGE,{"derivedFrom":subQ0}),1.0]])]});}
            var Q7;
            {var subQ0=sQuery(id+"F0.wireOp",EDGE,"E116");Q7=makeQuery(id+"F0.imprint","IMPRINT",FACE,{"disambiguationData":[TD([[makeQuery(id+"F0.imprint","IMPRINT",EDGE,{"derivedFrom":subQ0}),1.0]])]});}
            var Q8;
            {var subQ0=sQuery(id+"F0.wireOp",EDGE,"E115");var subQ1=sQuery(id+"F0.wireOp",EDGE,"E0");var subQ2=makeQuery(id+"F0.imprint","INTERSECT",VERTEX,{"derivedFrom":[subQ1,subQ0]});Q8=makeQuery(id+"F0.imprint","IMPRINT",FACE,{"disambiguationData":[TD([[makeQuery(id+"F0.imprint","IMPRINT",EDGE,{"disambiguationData":[TD([[subQ2,-1.0]])],"derivedFrom":subQ1}),-1.0]])]});}
            var Q9;
            {var subQ2=sQuery(id+"F0.wireOp",EDGE,"E15");Q9=makeQuery(id+"F0.imprint","IMPRINT",FACE,{"disambiguationData":[TD([[makeQuery(id+"F0.imprint","IMPRINT",EDGE,{"derivedFrom":subQ2}),1.0]])]});}
            var Q10;
            Q10=makeQuery(id+"F0.imprint","IMPRINT",FACE,{"disambiguationData":[TD([[makeQuery(id+"F0.imprint","IMPRINT",EDGE,{"derivedFrom":sQuery(id+"F0.wireOp",EDGE,"E49.bottom")}),1.0]])]});
            var Q11;
            Q11=makeQuery(id+"F0.imprint","IMPRINT",FACE,{"disambiguationData":[TD([[makeQuery(id+"F0.imprint","IMPRINT",EDGE,{"derivedFrom":sQuery(id+"F0.wireOp",EDGE,"E4")}),1.0]])]});
            var Q12;
            {var subQ0=sQuery(id+"F0.wireOp",EDGE,"E62");var subQ6=sQuery(id+"F0.wireOp",EDGE,"E60");var subQ9=makeQuery(id+"F0.imprint","INTERSECT",VERTEX,{"derivedFrom":[subQ6,subQ0]});Q12=makeQuery(id+"F0.imprint","IMPRINT",FACE,{"disambiguationData":[TD([[makeQuery(id+"F0.imprint","IMPRINT",EDGE,{"disambiguationData":[TD([[subQ9,-1.0]])],"derivedFrom":subQ6}),1.0]])]});}
            var Q13;
            {var subQ1=sQuery(id+"F0.wireOp",EDGE,"E46");var subQ5=makeQuery(id+"F0.imprint","INTERSECT",VERTEX,{"disambiguationData":[OD(0.0)],"derivedFrom":[subQ1,sQuery(id+"F0.wireOp",EDGE,"E47")]});Q13=makeQuery(id+"F0.imprint","IMPRINT",FACE,{"disambiguationData":[TD([[makeQuery(id+"F0.imprint","IMPRINT",EDGE,{"disambiguationData":[TD([[subQ5,1.0]])],"derivedFrom":subQ1}),1.0]])]});}
            var Q14;
            {var subQ0=sQuery(id+"F0.wireOp",EDGE,"E25");Q14=makeQuery(id+"F0.imprint","IMPRINT",FACE,{"disambiguationData":[TD([[makeQuery(id+"F0.imprint","IMPRINT",EDGE,{"derivedFrom":subQ0}),1.0]])]});}
            var Q15;
            {var subQ0=sQuery(id+"F0.wireOp",EDGE,"E16");Q15=makeQuery(id+"F0.imprint","IMPRINT",FACE,{"disambiguationData":[TD([[makeQuery(id+"F0.imprint","IMPRINT",EDGE,{"derivedFrom":subQ0}),1.0]])]});}
            var Q16;
            Q16=makeQuery(id+"F0.imprint","IMPRINT",FACE,{"disambiguationData":[TD([[makeQuery(id+"F0.imprint","IMPRINT",EDGE,{"derivedFrom":sQuery(id+"F0.wireOp",EDGE,"E17")}),-1.0]])]});
            var Q17;
            {var subQ0=sQuery(id+"F0.wireOp",EDGE,"E28");var subQ1=sQuery(id+"F0.wireOp",EDGE,"E12");var subQ2=makeQuery(id+"F0.imprint","INTERSECT",VERTEX,{"derivedFrom":[subQ1,subQ0]});Q17=makeQuery(id+"F0.imprint","IMPRINT",FACE,{"disambiguationData":[TD([[makeQuery(id+"F0.imprint","IMPRINT",EDGE,{"disambiguationData":[TD([[subQ2,-1.0]])],"derivedFrom":subQ1}),-1.0]])]});}
            var Q18;
            {var subQ0=sQuery(id+"F0.wireOp",EDGE,"E118");var subQ3=sQuery(id+"F0.wireOp",EDGE,"E12");var subQ4=makeQuery(id+"F0.imprint","INTERSECT",VERTEX,{"derivedFrom":[subQ3,subQ0]});Q18=makeQuery(id+"F0.imprint","IMPRINT",FACE,{"disambiguationData":[TD([[makeQuery(id+"F0.imprint","IMPRINT",EDGE,{"disambiguationData":[TD([[subQ4,-1.0]])],"derivedFrom":subQ3}),-1.0]])]});}
            var Q19;
            {var subQ5=sQuery(id+"F0.wireOp",EDGE,"E64");Q19=makeQuery(id+"F0.imprint","IMPRINT",FACE,{"disambiguationData":[TD([[makeQuery(id+"F0.imprint","IMPRINT",EDGE,{"derivedFrom":subQ5}),1.0]])]});}
            var Q20;
            {var subQ0=sQuery(id+"F0.wireOp",EDGE,"E48");var subQ1=sQuery(id+"F0.wireOp",EDGE,"E12");var subQ2=makeQuery(id+"F0.imprint","INTERSECT",VERTEX,{"derivedFrom":[subQ1,subQ0]});Q20=makeQuery(id+"F0.imprint","IMPRINT",FACE,{"disambiguationData":[TD([[makeQuery(id+"F0.imprint","IMPRINT",EDGE,{"disambiguationData":[TD([[subQ2,1.0]])],"derivedFrom":subQ1}),-1.0]])]});}
            var Q21;
            {var subQ3=sQuery(id+"F0.wireOp",EDGE,"E64");Q21=makeQuery(id+"F0.imprint","IMPRINT",FACE,{"disambiguationData":[TD([[makeQuery(id+"F0.imprint","IMPRINT",EDGE,{"derivedFrom":subQ3}),-1.0]])]});}
            var Q22;
            {var subQ5=sQuery(id+"F0.wireOp",EDGE,"E114");var subQ6=sQuery(id+"F0.wireOp",EDGE,"E0");var subQ7=makeQuery(id+"F0.imprint","INTERSECT",VERTEX,{"derivedFrom":[subQ6,subQ5]});Q22=makeQuery(id+"F0.imprint","IMPRINT",FACE,{"disambiguationData":[TD([[makeQuery(id+"F0.imprint","IMPRINT",EDGE,{"disambiguationData":[TD([[subQ7,-1.0]])],"derivedFrom":subQ6}),-1.0]])]});}
            var Q23;
            {var subQ5=sQuery(id+"F0.wireOp",EDGE,"E14");Q23=makeQuery(id+"F0.imprint","IMPRINT",FACE,{"disambiguationData":[TD([[makeQuery(id+"F0.imprint","IMPRINT",EDGE,{"derivedFrom":subQ5}),-1.0]])]});}
            var Q24;
            {var subQ0=sQuery(id+"F0.wireOp",EDGE,"E55");var subQ1=sQuery(id+"F0.wireOp",EDGE,"E12");var subQ2=makeQuery(id+"F0.imprint","INTERSECT",VERTEX,{"derivedFrom":[subQ1,subQ0]});Q24=makeQuery(id+"F0.imprint","IMPRINT",FACE,{"disambiguationData":[TD([[makeQuery(id+"F0.imprint","IMPRINT",EDGE,{"disambiguationData":[TD([[subQ2,1.0]])],"derivedFrom":subQ1}),-1.0]])]});}
            var Q25;
            {var subQ5=sQuery(id+"F0.wireOp",EDGE,"E16");Q25=makeQuery(id+"F0.imprint","IMPRINT",FACE,{"disambiguationData":[TD([[makeQuery(id+"F0.imprint","IMPRINT",EDGE,{"derivedFrom":subQ5}),-1.0]])]});}
            var Q26;
            {var subQ0=sQuery(id+"F0.wireOp",EDGE,"E61");var subQ1=sQuery(id+"F0.wireOp",EDGE,"E12");var subQ2=makeQuery(id+"F0.imprint","INTERSECT",VERTEX,{"derivedFrom":[subQ1,subQ0]});Q26=makeQuery(id+"F0.imprint","IMPRINT",FACE,{"disambiguationData":[TD([[makeQuery(id+"F0.imprint","IMPRINT",EDGE,{"disambiguationData":[TD([[subQ2,1.0]])],"derivedFrom":subQ1}),-1.0]])]});}
            var Q27;
            {var subQ0=sQuery(id+"F0.wireOp",EDGE,"E118");var subQ1=sQuery(id+"F0.wireOp",EDGE,"E0");var subQ2=makeQuery(id+"F0.imprint","INTERSECT",VERTEX,{"derivedFrom":[subQ1,subQ0]});Q27=makeQuery(id+"F0.imprint","IMPRINT",FACE,{"disambiguationData":[TD([[makeQuery(id+"F0.imprint","IMPRINT",EDGE,{"disambiguationData":[TD([[subQ2,-1.0]])],"derivedFrom":subQ1}),-1.0]])]});}
            var Q28;
            {var subQ0=sQuery(id+"F0.wireOp",EDGE,"E117");var subQ1=sQuery(id+"F0.wireOp",EDGE,"E54");var subQ2=makeQuery(id+"F0.imprint","INTERSECT",VERTEX,{"derivedFrom":[subQ1,subQ0]});Q28=makeQuery(id+"F0.imprint","IMPRINT",FACE,{"disambiguationData":[TD([[makeQuery(id+"F0.imprint","IMPRINT",EDGE,{"disambiguationData":[TD([[subQ2,-1.0]])],"derivedFrom":subQ1}),-1.0]])]});}
            var Q29;
            {var subQ0=sQuery(id+"F0.wireOp",EDGE,"E119");var subQ1=sQuery(id+"F0.wireOp",EDGE,"E54");var subQ2=makeQuery(id+"F0.imprint","INTERSECT",VERTEX,{"derivedFrom":[subQ1,subQ0]});Q29=makeQuery(id+"F0.imprint","IMPRINT",FACE,{"disambiguationData":[TD([[makeQuery(id+"F0.imprint","IMPRINT",EDGE,{"disambiguationData":[TD([[subQ2,-1.0]])],"derivedFrom":subQ1}),-1.0]])]});}
            var Q30;
            {var subQ0=sQuery(id+"F0.wireOp",EDGE,"E54");var subQ1=sQuery(id+"F0.wireOp",EDGE,"E46");var subQ2=makeQuery(id+"F0.imprint","INTERSECT",VERTEX,{"derivedFrom":[subQ1,subQ0]});Q30=makeQuery(id+"F0.imprint","IMPRINT",FACE,{"disambiguationData":[TD([[makeQuery(id+"F0.imprint","IMPRINT",EDGE,{"disambiguationData":[TD([[subQ2,1.0]])],"derivedFrom":subQ1}),1.0]])]});}
            var Q31;
            {var subQ0=sQuery(id+"F0.wireOp",EDGE,"E54");var subQ1=sQuery(id+"F0.wireOp",EDGE,"E12");var subQ2=makeQuery(id+"F0.imprint","INTERSECT",VERTEX,{"derivedFrom":[subQ1,subQ0]});Q31=makeQuery(id+"F0.imprint","IMPRINT",FACE,{"disambiguationData":[TD([[makeQuery(id+"F0.imprint","IMPRINT",EDGE,{"disambiguationData":[TD([[subQ2,1.0]])],"derivedFrom":subQ1}),-1.0]])]});}
            var Q32;
            {var subQ0=sQuery(id+"F0.wireOp",EDGE,"E60");var subQ3=makeQuery(id+"F0.imprint","INTERSECT",VERTEX,{"derivedFrom":[subQ0,sQuery(id+"F0.wireOp",EDGE,"E62")]});Q32=makeQuery(id+"F0.imprint","IMPRINT",FACE,{"disambiguationData":[TD([[makeQuery(id+"F0.imprint","IMPRINT",EDGE,{"disambiguationData":[TD([[subQ3,-1.0]])],"derivedFrom":subQ0}),-1.0]])]});}
            var Q33;
            {var subQ0=sQuery(id+"F0.wireOp",EDGE,"E119");var subQ1=sQuery(id+"F0.wireOp",EDGE,"E54");var subQ2=makeQuery(id+"F0.imprint","INTERSECT",VERTEX,{"derivedFrom":[subQ1,subQ0]});Q33=makeQuery(id+"F0.imprint","IMPRINT",FACE,{"disambiguationData":[TD([[makeQuery(id+"F0.imprint","IMPRINT",EDGE,{"disambiguationData":[TD([[subQ2,-1.0]])],"derivedFrom":subQ1}),1.0]])]});}
            var Q34;
            {var subQ0=sQuery(id+"F0.wireOp",EDGE,"E30");var subQ1=makeQuery(id+"F0.imprint","INTERSECT",VERTEX,{"derivedFrom":[sQuery(id+"F0.wireOp",EDGE,"E13"),subQ0]});Q34=makeQuery(id+"F0.imprint","IMPRINT",FACE,{"disambiguationData":[TD([[makeQuery(id+"F0.imprint","IMPRINT",EDGE,{"disambiguationData":[TD([[subQ1,1.0]])],"derivedFrom":subQ0}),1.0]])]});}
            var Q35;
            {var subQ0=sQuery(id+"F0.wireOp",EDGE,"E63");var subQ1=makeQuery(id+"F0.imprint","INTERSECT",VERTEX,{"derivedFrom":[sQuery(id+"F0.wireOp",EDGE,"E61"),subQ0]});Q35=makeQuery(id+"F0.imprint","IMPRINT",FACE,{"disambiguationData":[TD([[makeQuery(id+"F0.imprint","IMPRINT",EDGE,{"disambiguationData":[TD([[subQ1,-1.0]])],"derivedFrom":subQ0}),1.0]])]});}
            var Q36;
            {var subQ0=sQuery(id+"F0.wireOp",EDGE,"E29");var subQ1=sQuery(id+"F0.wireOp",EDGE,"E13");var subQ2=makeQuery(id+"F0.imprint","INTERSECT",VERTEX,{"derivedFrom":[subQ1,subQ0]});Q36=makeQuery(id+"F0.imprint","IMPRINT",FACE,{"disambiguationData":[TD([[makeQuery(id+"F0.imprint","IMPRINT",EDGE,{"disambiguationData":[TD([[subQ2,1.0]])],"derivedFrom":subQ1}),-1.0]])]});}
            var Q37;
            {var subQ0=sQuery(id+"F0.wireOp",EDGE,"E62");var subQ1=sQuery(id+"F0.wireOp",EDGE,"E61");var subQ2=makeQuery(id+"F0.imprint","INTERSECT",VERTEX,{"derivedFrom":[subQ1,subQ0]});Q37=makeQuery(id+"F0.imprint","IMPRINT",FACE,{"disambiguationData":[TD([[makeQuery(id+"F0.imprint","IMPRINT",EDGE,{"disambiguationData":[TD([[subQ2,1.0]])],"derivedFrom":subQ1}),-1.0]])]});}
            var Q38;
            {var subQ3=sQuery(id+"F0.wireOp",EDGE,"E68");Q38=makeQuery(id+"F0.imprint","IMPRINT",FACE,{"disambiguationData":[TD([[makeQuery(id+"F0.imprint","IMPRINT",EDGE,{"derivedFrom":subQ3}),-1.0]])]});}
            extrude(context, id + "F2", {"entities" : qUnion([Q0, Q1, Q2, Q3, Q4, Q5, Q6, Q7, Q8, Q9, Q10, Q11, Q12, Q13, Q14, Q15, Q16, Q17, Q18, Q19, Q20, Q21, Q22, Q23, Q24, Q25, Q26, Q27, Q28, Q29, Q30, Q31, Q32, Q33, Q34, Q35, Q36, Q37, Q38]), "depth" : 50 * mm, "hasSecondDirection" : true, "secondDirectionOppositeDirection" : true, "secondDirectionDepth" : 50 * mm});
        }
        {
            var Q0;
            Q0=makeQuery(id+"F2.opExtrude","SWEPT_FACE",FACE,{"disambiguationData":[OSD([sQuery(id+"F0.wireOp",EDGE,"E0"),sQuery(id+"F0.wireOp",EDGE,"E73")])]});
            var sketch = newSketch(context, id + "F3", { "sketchPlane" : qUnion([Q0])});
            skLineSegment(sketch, "E120", {"start": v(0, -181.67) * mm, "end": v(0, 153.75) * mm});
            skLineSegment(sketch, "E121", {"start": v(0, -181.67) * mm, "end": v(-22.98, -181.67) * mm});
            skLineSegment(sketch, "E122", {"start": v(0.11, 153.75) * mm, "end": v(0, 153.75) * mm});
            skLineSegment(sketch, "E123", {"start": v(-2.86, 151.16) * mm, "end": v(-21.56, 16.57) * mm});
            skPoint(sketch, "E124.visualSharp", {"position": v(-2.5, 153.75) * mm});
            skArc(sketch, "E124.filletArc", {"start": v(0.11, 153.75) * mm, "mid": v(-1.86, 153.01) * mm, "end": v(-2.86, 151.16) * mm});
            skFitSpline(sketch, "E125", {"points": [v(-21.56, 16.57) * mm, v(-23.97, -5.24) * mm, v(-25.6, -40.82) * mm, v(-26.06, -88.98) * mm, v(-26.06, -114.54) * mm, v(-24.28, -158.34) * mm, v(-22.98, -181.67) * mm, v(-20.26, -202.56) * mm, v(-15.93, -219.98) * mm, v(-11.68, -228.16) * mm], "startDerivative": vector(-27.25, -204) * mm, "endDerivative": vector(67.27, -110.48) * mm});
            skFitSpline(sketch, "E126", {"points": [v(-18.48, -181.67) * mm, v(-16.77, -196.36) * mm, v(-14.8, -212.1) * mm, v(-13.16, -221.12) * mm, v(-11.68, -228.16) * mm], "startDerivative": vector(3.95, -50.37) * mm, "endDerivative": vector(7.5, -35.11) * mm});
            skLineSegment(sketch, "E127.MirrorCS", {"start": v(-0.11, 153.75) * mm, "end": v(0, 153.75) * mm});
            skLineSegment(sketch, "E128", {"start": v(0, -179.67) * mm, "end": v(-23.15, -179.67) * mm});
            skLineSegment(sketch, "E129", {"start": v(-1.01, 153.53) * mm, "end": v(-20.08, 16.31) * mm});
            skFitSpline(sketch, "E130", {"points": [v(-21.65, -179.67) * mm, v(-22.78, -158.29) * mm, v(-24.56, -114.6) * mm, v(-24.56, -88.95) * mm, v(-24.1, -40.87) * mm, v(-22.48, -5.37) * mm, v(-20.08, 16.31) * mm], "startDerivative": vector(-7.77, 136.79) * mm, "endDerivative": vector(18.24, 150.25) * mm});
            skLineSegment(sketch, "E131", {"start": v(0, 139.03) * mm, "end": v(-17.1, 15.9) * mm});
            skFitSpline(sketch, "E132", {"points": [v(-17.1, 15.9) * mm, v(-19.48, -5.54) * mm, v(-21.1, -40.85) * mm, v(-21.56, -88.95) * mm, v(-21.56, -114.6) * mm, v(-19.78, -158.29) * mm, v(-18.65, -179.67) * mm], "startDerivative": vector(-16.66, -149.96) * mm, "endDerivative": vector(5.99, -136.68) * mm});
            skFitSpline(sketch, "E133", {"points": [v(-21.48, -181.67) * mm, v(-19.07, -202.4) * mm, v(-15.26, -219.8) * mm, v(-11.68, -228.16) * mm], "startDerivative": vector(4.75, -53.64) * mm, "endDerivative": vector(14.48, -29.4) * mm});
            skArc(sketch, "E134.MirrorCS", {"start": v(-0.11, 153.75) * mm, "mid": v(1.86, 153.01) * mm, "end": v(2.86, 151.16) * mm});
            skFitSpline(sketch, "E135.MirrorCS", {"points": [v(21.48, -181.67) * mm, v(19.07, -202.4) * mm, v(15.26, -219.8) * mm, v(11.68, -228.16) * mm], "startDerivative": vector(-4.75, -53.64) * mm, "endDerivative": vector(-14.48, -29.4) * mm});
            skFitSpline(sketch, "E136.MirrorCS", {"points": [v(18.48, -181.67) * mm, v(16.77, -196.36) * mm, v(14.8, -212.1) * mm, v(13.16, -221.12) * mm, v(11.68, -228.16) * mm], "startDerivative": vector(-3.95, -50.37) * mm, "endDerivative": vector(-7.5, -35.11) * mm});
            skLineSegment(sketch, "E137.MirrorCS", {"start": v(0, -179.67) * mm, "end": v(23.15, -179.67) * mm});
            skLineSegment(sketch, "E138.MirrorCS", {"start": v(2.86, 151.16) * mm, "end": v(21.56, 16.57) * mm});
            skLineSegment(sketch, "E139.MirrorCS", {"start": v(0, 139.03) * mm, "end": v(17.1, 15.9) * mm});
            skPoint(sketch, "E140.MirrorP", {"position": v(2.5, 153.75) * mm});
            skFitSpline(sketch, "E141.MirrorCS", {"points": [v(17.1, 15.9) * mm, v(19.48, -5.54) * mm, v(21.1, -40.85) * mm, v(21.56, -88.95) * mm, v(21.56, -114.6) * mm, v(19.78, -158.29) * mm, v(18.65, -179.67) * mm], "startDerivative": vector(16.66, -149.96) * mm, "endDerivative": vector(-5.99, -136.68) * mm});
            skLineSegment(sketch, "E142.MirrorCS", {"start": v(1.01, 153.53) * mm, "end": v(20.08, 16.31) * mm});
            skLineSegment(sketch, "E143.MirrorCS", {"start": v(0, -181.67) * mm, "end": v(22.98, -181.67) * mm});
            skFitSpline(sketch, "E144.MirrorCS", {"points": [v(21.56, 16.57) * mm, v(23.97, -5.24) * mm, v(25.6, -40.82) * mm, v(26.06, -88.98) * mm, v(26.06, -114.54) * mm, v(24.28, -158.34) * mm, v(22.98, -181.67) * mm, v(20.26, -202.56) * mm, v(15.93, -219.98) * mm, v(11.68, -228.16) * mm], "startDerivative": vector(27.25, -204) * mm, "endDerivative": vector(-67.27, -110.48) * mm});
            skFitSpline(sketch, "E145.MirrorCS", {"points": [v(21.65, -179.67) * mm, v(22.78, -158.29) * mm, v(24.56, -114.6) * mm, v(24.56, -88.95) * mm, v(24.1, -40.87) * mm, v(22.48, -5.37) * mm, v(20.08, 16.31) * mm], "startDerivative": vector(7.77, 136.79) * mm, "endDerivative": vector(-18.24, 150.25) * mm});
            skSolve(sketch);
        }
        {
            var Q0;
            {var subQ0=sQuery(id+"F3.wireOp",EDGE,"E122");Q0=makeQuery(id+"F3.imprint","IMPRINT",FACE,{"disambiguationData":[TD([[makeQuery(id+"F3.imprint","IMPRINT",EDGE,{"derivedFrom":subQ0}),1.0]])]});}
            var Q1;
            {var subQ0=sQuery(id+"F3.wireOp",EDGE,"E127.MirrorCS");Q1=makeQuery(id+"F3.imprint","IMPRINT",FACE,{"disambiguationData":[TD([[makeQuery(id+"F3.imprint","IMPRINT",EDGE,{"derivedFrom":subQ0}),1.0]])]});}
            var Q2;
            {var subQ4=sQuery(id+"F3.wireOp",EDGE,"E123");Q2=makeQuery(id+"F3.imprint","IMPRINT",FACE,{"disambiguationData":[TD([[makeQuery(id+"F3.imprint","IMPRINT",EDGE,{"derivedFrom":subQ4}),1.0]])]});}
            var Q3;
            {var subQ1=sQuery(id+"F3.wireOp",EDGE,"E138.MirrorCS");Q3=makeQuery(id+"F3.imprint","IMPRINT",FACE,{"disambiguationData":[TD([[makeQuery(id+"F3.imprint","IMPRINT",EDGE,{"derivedFrom":subQ1}),-1.0]])]});}
            var Q4;
            {var subQ1=sQuery(id+"F3.wireOp",EDGE,"E121");var subQ9=makeQuery(id+"F3.imprint","INTERSECT",VERTEX,{"derivedFrom":[subQ1,sQuery(id+"F3.wireOp",EDGE,"E126")]});Q4=makeQuery(id+"F3.imprint","IMPRINT",FACE,{"disambiguationData":[TD([[makeQuery(id+"F3.imprint","IMPRINT",EDGE,{"disambiguationData":[TD([[subQ9,-1.0]])],"derivedFrom":subQ1}),-1.0]])]});}
            var Q5;
            {var subQ1=sQuery(id+"F3.wireOp",EDGE,"E137.MirrorCS");var subQ4=makeQuery(id+"F3.imprint","INTERSECT",VERTEX,{"derivedFrom":[subQ1,sQuery(id+"F3.wireOp",EDGE,"E141.MirrorCS")]});Q5=makeQuery(id+"F3.imprint","IMPRINT",FACE,{"disambiguationData":[TD([[makeQuery(id+"F3.imprint","IMPRINT",EDGE,{"disambiguationData":[TD([[subQ4,-1.0]])],"derivedFrom":subQ1}),-1.0]])]});}
            var Q6;
            {var subQ0=sQuery(id+"F3.wireOp",EDGE,"E133");var subQ1=sQuery(id+"F3.wireOp",EDGE,"E125");var subQ2=makeQuery(id+"F3.imprint","INTERSECT",VERTEX,{"derivedFrom":[subQ1,sQuery(id+"F3.wireOp",EDGE,"E126"),subQ0]});Q6=makeQuery(id+"F3.imprint","IMPRINT",FACE,{"disambiguationData":[TD([[makeQuery(id+"F3.imprint","IMPRINT",EDGE,{"disambiguationData":[TD([[subQ2,1.0]])],"derivedFrom":subQ1}),1.0]])]});}
            var Q7;
            {var subQ0=sQuery(id+"F3.wireOp",EDGE,"E144.MirrorCS");var subQ1=sQuery(id+"F3.wireOp",EDGE,"E135.MirrorCS");var subQ2=makeQuery(id+"F3.imprint","INTERSECT",VERTEX,{"derivedFrom":[subQ1,sQuery(id+"F3.wireOp",EDGE,"E136.MirrorCS"),subQ0]});Q7=makeQuery(id+"F3.imprint","IMPRINT",FACE,{"disambiguationData":[TD([[makeQuery(id+"F3.imprint","IMPRINT",EDGE,{"disambiguationData":[TD([[subQ2,1.0]])],"derivedFrom":subQ1}),1.0]])]});}
            var Q8;
            {var subQ0=sQuery(id+"F3.wireOp",EDGE,"E125");var subQ1=sQuery(id+"F3.wireOp",EDGE,"E121");var subQ2=makeQuery(id+"F3.imprint","INTERSECT",VERTEX,{"derivedFrom":[subQ1,subQ0]});Q8=makeQuery(id+"F3.imprint","IMPRINT",FACE,{"disambiguationData":[TD([[makeQuery(id+"F3.imprint","IMPRINT",EDGE,{"disambiguationData":[TD([[subQ2,1.0]])],"derivedFrom":subQ1}),1.0]])]});}
            var Q9;
            {var subQ0=sQuery(id+"F3.wireOp",EDGE,"E143.MirrorCS");var subQ1=sQuery(id+"F3.wireOp",EDGE,"E135.MirrorCS");var subQ2=makeQuery(id+"F3.imprint","INTERSECT",VERTEX,{"derivedFrom":[subQ1,subQ0]});Q9=makeQuery(id+"F3.imprint","IMPRINT",FACE,{"disambiguationData":[TD([[makeQuery(id+"F3.imprint","IMPRINT",EDGE,{"disambiguationData":[TD([[subQ2,-1.0]])],"derivedFrom":subQ0}),-1.0]])]});}
            extrude(context, id + "F4", {"entities" : qUnion([Q0, Q1, Q2, Q3, Q4, Q5, Q6, Q7, Q8, Q9]), "operationType" : NewBodyOperationType.INTERSECT, "oppositeDirection" : true, "depth" : 60 * mm});
        }
        {
            var Q0;
            {var subQ3=sQuery(id+"F0.wireOp",EDGE,"E64");Q0=makeQuery(id+"F0.imprint","IMPRINT",FACE,{"disambiguationData":[TD([[makeQuery(id+"F0.imprint","IMPRINT",EDGE,{"derivedFrom":subQ3}),-1.0]])]});}
            var Q1;
            {var subQ0=sQuery(id+"F0.wireOp",EDGE,"E68");Q1=makeQuery(id+"F0.imprint","IMPRINT",FACE,{"disambiguationData":[TD([[makeQuery(id+"F0.imprint","IMPRINT",EDGE,{"derivedFrom":subQ0}),1.0]])]});}
            var Q2;
            {var subQ0=sQuery(id+"F0.wireOp",EDGE,"E73");Q2=makeQuery(id+"F0.imprint","IMPRINT",FACE,{"disambiguationData":[TD([[makeQuery(id+"F0.imprint","IMPRINT",EDGE,{"derivedFrom":subQ0}),1.0]])]});}
            var Q3;
            {var subQ3=sQuery(id+"F0.wireOp",EDGE,"E68");Q3=makeQuery(id+"F0.imprint","IMPRINT",FACE,{"disambiguationData":[TD([[makeQuery(id+"F0.imprint","IMPRINT",EDGE,{"derivedFrom":subQ3}),-1.0]])]});}
            var Q4;
            {var subQ5=sQuery(id+"F0.wireOp",EDGE,"E114");var subQ6=sQuery(id+"F0.wireOp",EDGE,"E0");var subQ7=makeQuery(id+"F0.imprint","INTERSECT",VERTEX,{"derivedFrom":[subQ6,subQ5]});Q4=makeQuery(id+"F0.imprint","IMPRINT",FACE,{"disambiguationData":[TD([[makeQuery(id+"F0.imprint","IMPRINT",EDGE,{"disambiguationData":[TD([[subQ7,-1.0]])],"derivedFrom":subQ6}),-1.0]])]});}
            var Q5;
            {var subQ0=sQuery(id+"F0.wireOp",EDGE,"E115");var subQ1=sQuery(id+"F0.wireOp",EDGE,"E0");var subQ2=makeQuery(id+"F0.imprint","INTERSECT",VERTEX,{"derivedFrom":[subQ1,subQ0]});Q5=makeQuery(id+"F0.imprint","IMPRINT",FACE,{"disambiguationData":[TD([[makeQuery(id+"F0.imprint","IMPRINT",EDGE,{"disambiguationData":[TD([[subQ2,-1.0]])],"derivedFrom":subQ1}),-1.0]])]});}
            var Q6;
            {var subQ0=sQuery(id+"F0.wireOp",EDGE,"E118");var subQ1=sQuery(id+"F0.wireOp",EDGE,"E0");var subQ2=makeQuery(id+"F0.imprint","INTERSECT",VERTEX,{"derivedFrom":[subQ1,subQ0]});Q6=makeQuery(id+"F0.imprint","IMPRINT",FACE,{"disambiguationData":[TD([[makeQuery(id+"F0.imprint","IMPRINT",EDGE,{"disambiguationData":[TD([[subQ2,-1.0]])],"derivedFrom":subQ1}),-1.0]])]});}
            var Q7;
            {var subQ8=sQuery(id+"F0.wireOp",EDGE,"E0");var subQ12=makeQuery(id+"F0.imprint","INTERSECT",VERTEX,{"derivedFrom":[subQ8,sQuery(id+"F0.wireOp",EDGE,"E70")]});Q7=makeQuery(id+"F0.imprint","IMPRINT",FACE,{"disambiguationData":[TD([[makeQuery(id+"F0.imprint","IMPRINT",EDGE,{"disambiguationData":[TD([[subQ12,1.0]])],"derivedFrom":subQ8}),-1.0]])]});}
            var Q8;
            {var subQ0=sQuery(id+"F0.wireOp",EDGE,"E28");var subQ1=sQuery(id+"F0.wireOp",EDGE,"E12");var subQ2=makeQuery(id+"F0.imprint","INTERSECT",VERTEX,{"derivedFrom":[subQ1,subQ0]});Q8=makeQuery(id+"F0.imprint","IMPRINT",FACE,{"disambiguationData":[TD([[makeQuery(id+"F0.imprint","IMPRINT",EDGE,{"disambiguationData":[TD([[subQ2,-1.0]])],"derivedFrom":subQ1}),-1.0]])]});}
            var Q9;
            {var subQ5=sQuery(id+"F0.wireOp",EDGE,"E14");Q9=makeQuery(id+"F0.imprint","IMPRINT",FACE,{"disambiguationData":[TD([[makeQuery(id+"F0.imprint","IMPRINT",EDGE,{"derivedFrom":subQ5}),-1.0]])]});}
            var Q10;
            {var subQ0=sQuery(id+"F0.wireOp",EDGE,"E25");Q10=makeQuery(id+"F0.imprint","IMPRINT",FACE,{"disambiguationData":[TD([[makeQuery(id+"F0.imprint","IMPRINT",EDGE,{"derivedFrom":subQ0}),1.0]])]});}
            var Q11;
            {var subQ5=sQuery(id+"F0.wireOp",EDGE,"E16");Q11=makeQuery(id+"F0.imprint","IMPRINT",FACE,{"disambiguationData":[TD([[makeQuery(id+"F0.imprint","IMPRINT",EDGE,{"derivedFrom":subQ5}),-1.0]])]});}
            extrude(context, id + "F5", {"entities" : qUnion([Q0, Q1, Q2, Q3, Q4, Q5, Q6, Q7, Q8, Q9, Q10, Q11]), "depth" : 50 * mm, "hasSecondDirection" : true, "secondDirectionOppositeDirection" : true, "secondDirectionDepth" : 50 * mm});
        }
        {
            var Q0;
            {var subQ0=sQuery(id+"F3.wireOp",EDGE,"E126");var subQ1=sQuery(id+"F3.wireOp",EDGE,"E121");var subQ2=makeQuery(id+"F3.imprint","INTERSECT",VERTEX,{"derivedFrom":[subQ1,subQ0]});Q0=makeQuery(id+"F3.imprint","IMPRINT",FACE,{"disambiguationData":[TD([[makeQuery(id+"F3.imprint","IMPRINT",EDGE,{"disambiguationData":[TD([[subQ2,-1.0]])],"derivedFrom":subQ1}),1.0]])]});}
            var Q1;
            {var subQ0=sQuery(id+"F3.wireOp",EDGE,"E129");Q1=makeQuery(id+"F3.imprint","IMPRINT",FACE,{"disambiguationData":[TD([[makeQuery(id+"F3.imprint","IMPRINT",EDGE,{"derivedFrom":subQ0}),1.0]])]});}
            var Q2;
            {var subQ3=sQuery(id+"F3.wireOp",EDGE,"E139.MirrorCS");Q2=makeQuery(id+"F3.imprint","IMPRINT",FACE,{"disambiguationData":[TD([[makeQuery(id+"F3.imprint","IMPRINT",EDGE,{"derivedFrom":subQ3}),1.0]])]});}
            var Q3;
            {var subQ0=sQuery(id+"F3.wireOp",EDGE,"E143.MirrorCS");var subQ1=sQuery(id+"F3.wireOp",EDGE,"E135.MirrorCS");var subQ2=makeQuery(id+"F3.imprint","INTERSECT",VERTEX,{"derivedFrom":[subQ1,subQ0]});Q3=makeQuery(id+"F3.imprint","IMPRINT",FACE,{"disambiguationData":[TD([[makeQuery(id+"F3.imprint","IMPRINT",EDGE,{"disambiguationData":[TD([[subQ2,1.0]])],"derivedFrom":subQ0}),-1.0]])]});}
            var Q4;
            {var subQ0=sQuery(id+"F3.wireOp",EDGE,"E133");var subQ1=sQuery(id+"F3.wireOp",EDGE,"E126");var subQ2=makeQuery(id+"F3.imprint","INTERSECT",VERTEX,{"derivedFrom":[sQuery(id+"F3.wireOp",EDGE,"E125"),subQ1,subQ0]});Q4=makeQuery(id+"F3.imprint","IMPRINT",FACE,{"disambiguationData":[TD([[makeQuery(id+"F3.imprint","IMPRINT",EDGE,{"disambiguationData":[TD([[subQ2,1.0]])],"derivedFrom":subQ1}),-1.0]])]});}
            var Q5;
            {var subQ0=sQuery(id+"F3.wireOp",EDGE,"E136.MirrorCS");var subQ1=sQuery(id+"F3.wireOp",EDGE,"E135.MirrorCS");var subQ2=makeQuery(id+"F3.imprint","INTERSECT",VERTEX,{"derivedFrom":[subQ1,subQ0,sQuery(id+"F3.wireOp",EDGE,"E144.MirrorCS")]});Q5=makeQuery(id+"F3.imprint","IMPRINT",FACE,{"disambiguationData":[TD([[makeQuery(id+"F3.imprint","IMPRINT",EDGE,{"disambiguationData":[TD([[subQ2,1.0]])],"derivedFrom":subQ1}),-1.0]])]});}
            extrude(context, id + "F6", {"entities" : qUnion([Q0, Q1, Q2, Q3, Q4, Q5]), "operationType" : NewBodyOperationType.INTERSECT, "oppositeDirection" : true, "depth" : 60 * mm});
        }
    });
